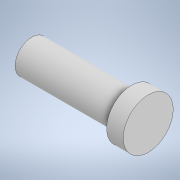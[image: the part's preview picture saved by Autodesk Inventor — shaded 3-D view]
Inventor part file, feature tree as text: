
AUTODESK INVENTOR PART (.ipt)
format: ipt  version: 2022 (Build 260153070, 153G)  size: 101,888 bytes
history: native  units: mm
features: extrude x2, sketch x2
ambient origin geometry x8: Origin, YZ Plane, XZ Plane, XY Plane, X Axis, Y Axis, Z Axis, Center Point
bodies: Solid1 (feature_tree)
feature tree (4):
  extrude  "Extrusion1"  Depth=6.0mm TaperAngle=0.0deg
  extrude  "Extrusion2"  Depth=1.0mm TaperAngle=0.0deg
  sketch  "Sketch1"  dims[d0=2.0mm d1=6.0mm d2=0.0mm]
  sketch  "Sketch2"  dims[d3=3.0mm d4=1.0mm d5=0.0mm]
